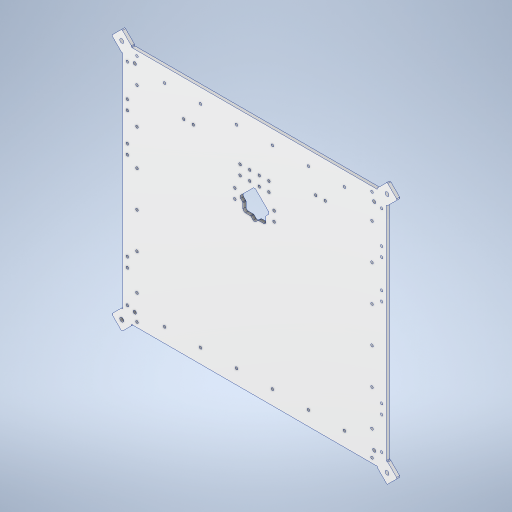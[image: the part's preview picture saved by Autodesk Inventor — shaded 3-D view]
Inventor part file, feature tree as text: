
AUTODESK INVENTOR PART (.ipt)
format: ipt  version: 2024 (Build 280153000, 153)  size: 557,568 bytes
history: native  units: mm
features: sketch x7, hole x6, mirror x4, extrude x3, fillet x1, projected_geometry x1
ambient origin geometry x8: Origin, YZ Plane, XZ Plane, XY Plane, X Axis, Y Axis, Z Axis, Center Point
bodies: Solid1 (feature_tree)
feature tree (22):
  extrude  "Extrusion1"  Depth=500.0mm
  hole  "Hole1"  [1 undecoded]
  sketch  "Sketch3"  dims[d5=40.0mm d6=40.0mm]
  hole  "Hole2"  [1 undecoded]
  extrude  "Extrusion5"  Depth=80.0mm
  sketch  "Sketch4"  dims[d7=40.0mm d8=80.0mm]
  extrude  "Extrusion2"  Depth=40.0mm
  fillet  "Fillet2"  Radius=40.0mm
  hole  "Hole6"  [1 undecoded]
  mirror  "Mirror1"
  mirror  "Mirror2"
  hole  "Hole4"  [1 undecoded]
  mirror  "Mirror3"
  hole  "Hole7"  [1 undecoded]
  mirror  "Mirror4"
  hole  "Hole5"  [1 undecoded]
  sketch  "Sketch1"  dims[d0=550.0mm d1=500.0mm]
  sketch  "Sketch2"  dims[d2=6.35mm d3=0.0mm d4=40.0mm]
  projected_geometry  "Projected Loop1"
  sketch  "Sketch7"  dims[d9=40.0mm d10=40.0mm d11=40.0mm]
  sketch  "Sketch8"  dims[d13=40.0mm d14=40.0mm]
  sketch  "Sketch9"  dims[d15=20.0mm d16=40.0mm d17=20.0mm d18=40.0mm d19=40.0mm d20=20.0mm d21=40.0mm d22=20.0mm d23=3.0mm d24=275.0mm d25=20.0mm d26=40.0mm d27=20.0mm d28=40.0mm d29=20.0mm d30=40.0mm d31=20.0mm d32=40.0mm d33=392.0mm d35=10.0mm d36=10.0mm d37=88.0mm d40=88.0mm d42=48.0mm d44=164.0mm d49=10.0mm d51=162.0mm d52=20.0mm d53=20.0mm d54=20.0mm d55=20.0mm d56=20.0mm d57=20.0mm d58=20.0mm d59=20.0mm d60=20.0mm d61=20.0mm d62=20.0mm d63=20.0mm d64=20.0mm d65=20.0mm d66=20.0mm d67=20.0mm d68=20.0mm d69=20.0mm d70=60.0mm d71=20.0mm d72=5.3mm d73=6.0mm d74=4.0mm d75=2.0mm d76=90.0deg d77=8.0mm d78=20.594885mm d79=10.0mm d87=80.0mm d88=82.0mm d89=20.0mm d90=28.0mm d91=5.3mm d92=6.0mm d93=4.0mm d94=2.0mm d95=90.0deg d96=8.0mm d97=20.594885mm d100=6.35mm d101=0.0mm d118=490.0mm d119=440.0mm d128=5.3mm d129=6.0mm d130=4.0mm d131=2.0mm d132=90.0deg d133=8.0mm d134=20.594885mm d138=499.0mm d139=449.0mm d140=13.0mm d141=6.647mm d142=16.0mm d143=4.0mm d144=2.0mm d145=90.0deg d146=22.2mm d147=150.0deg d156=20.0mm d157=23.0mm d158=23.0mm d159=20.0mm d160=30.0mm d161=30.0mm d162=2.0mm d163=2.0mm d164=8.3mm d165=6.0mm d166=10.0mm d167=5.0mm d168=90.0deg d169=8.0mm d170=0.0mm d175=440.0mm d176=60.0mm d178=75.0mm d179=10.0mm d181=10.0mm d183=375.0mm d184=5.3mm d185=6.0mm d186=4.0mm d187=2.0mm d188=90.0deg d189=8.0mm d190=0.0mm d192=60.0mm d194=75.0mm d195=10.0mm d197=10.0mm d200=375.0mm d201=45.0mm d202=4.0mm d203=0.0mm d204=0.0mm d205=48.0mm d206=48.0mm d207=5.0mm d208=2.0mm]
note: 6 required parameter values undecoded (feature->parameter linkage not recoverable at this tier; creation-order binding heuristic only, values carry confidence <= 0.55)
